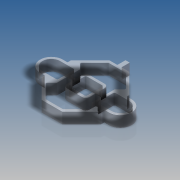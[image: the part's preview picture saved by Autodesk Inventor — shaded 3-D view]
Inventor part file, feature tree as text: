
AUTODESK INVENTOR PART (.ipt)
format: ipt  version: 2016 SP2 (Build 200236200, 236)  size: 461,312 bytes
history: native  units: in
note: dims shown in document units (in); Inventor stores cm internally (conversion verified against a paired STEP export)
features: extrude x1, fillet x1, sketch x1
ambient origin geometry x8: Origin, YZ Plane, XZ Plane, XY Plane, X Axis, Y Axis, Z Axis, Center Point
bodies: Solid1 (feature_tree)
feature tree (3):
  extrude  "Extrusion1"  Depth=0.0236in
  fillet  "Fillet1"  Radius=0.0236in
  sketch  "Sketch2"  dims[d0=0.0236in d1=0.0236in d2=0.0236in d3=0.3213in d4=0.0472in d5=0.0472in d6=0.1071in d7=0.422in d8=0.0472in d9=0.0472in d10=0.2677in d11=0.4157in d12=1.0866in d13=0.5197in d14=1.2441in d15=0.622in d16=0.378in d17=0.0472in d18=0.315in d19=0.0787in d20=0.1496in d21=0.2047in d22=0.0in d23=0.0039in]
